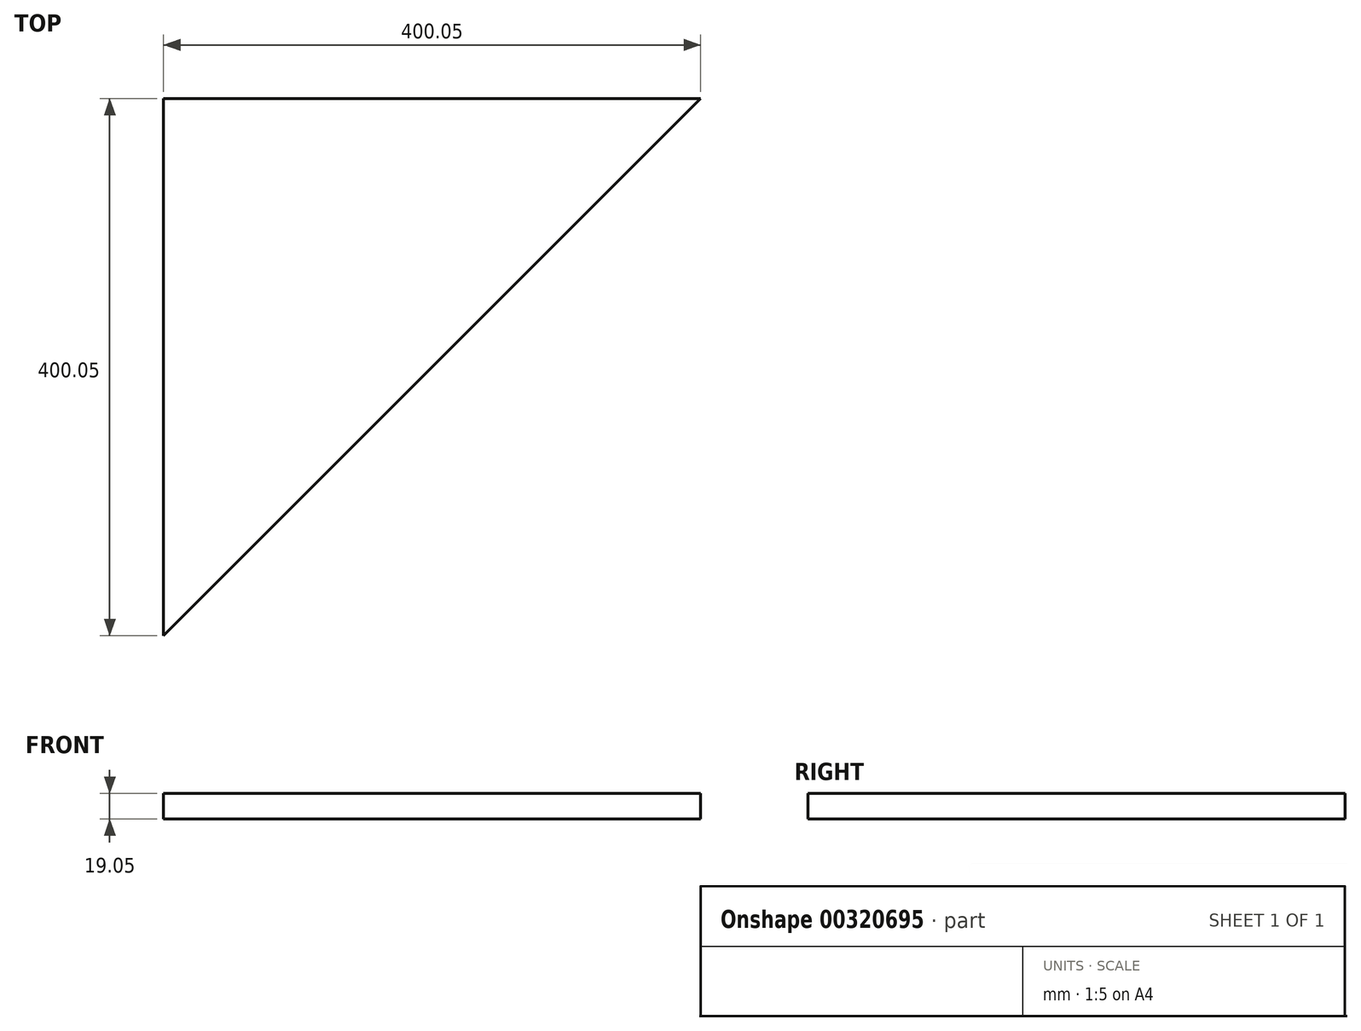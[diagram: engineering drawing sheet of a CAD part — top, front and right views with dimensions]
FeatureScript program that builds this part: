
annotation { "Feature Type Name" : "Feature", "Feature Type Description" : "" }
export const myFeature = defineFeature(function(context is Context, id is Id, definition is map)
    precondition{}
    {
        {
            var Q0;
            Q0=qCreatedBy(makeId("Top.planeOp"),FACE);
            var sketch = newSketch(context, id + "F0", { "sketchPlane" : qUnion([Q0])});
            skLineSegment(sketch, "E0", {"start": v(-40.72, 213.98) * mm, "end": v(-40.72, -186.07) * mm});
            skLineSegment(sketch, "E1", {"start": v(-40.72, 213.98) * mm, "end": v(359.33, 213.98) * mm});
            skLineSegment(sketch, "E2", {"start": v(359.33, 213.98) * mm, "end": v(-40.72, -186.07) * mm});
            skSolve(sketch);
        }
        {
            var Q0;
            Q0 = qSketchRegion(id + "F0", true);
            extrude(context, id + "F1", {"entities" : qUnion([Q0]), "depth" : 19.05 * mm});
        }
    });
